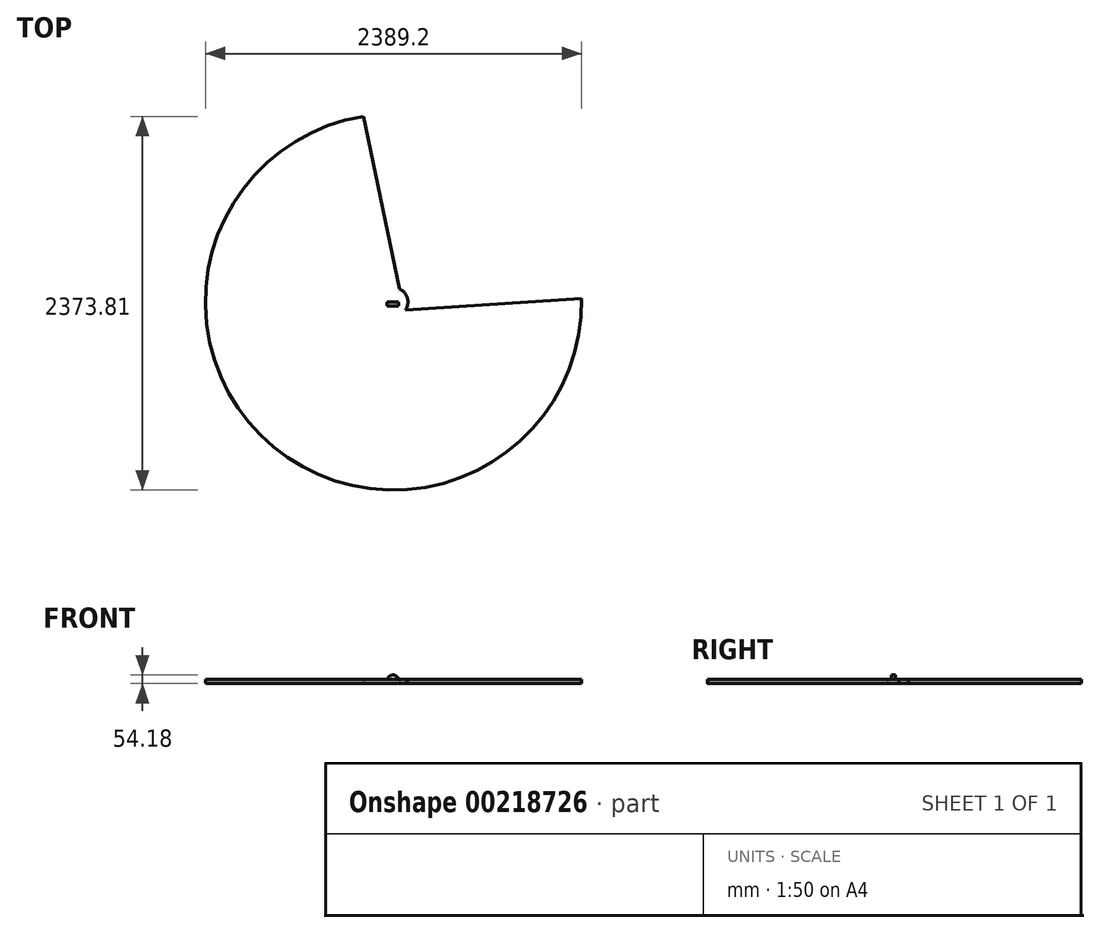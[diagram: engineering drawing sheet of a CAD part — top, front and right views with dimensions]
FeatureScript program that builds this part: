
annotation { "Feature Type Name" : "Feature", "Feature Type Description" : "" }
export const myFeature = defineFeature(function(context is Context, id is Id, definition is map)
    precondition{}
    {
        {
            var Q0;
            Q0=qCreatedBy(makeId("Front.planeOp"),FACE);
            var sketch = newSketch(context, id + "F0", { "sketchPlane" : qUnion([Q0])});
            skLineSegment(sketch, "E0", {"start": v(-39.47, 0) * mm, "end": v(-39.47, 19.73) * mm});
            skLineSegment(sketch, "E1", {"start": v(-39.47, 19.73) * mm, "end": v(-34.07, 19.73) * mm});
            skLineSegment(sketch, "E2", {"start": v(-34.07, 19.73) * mm, "end": v(-34.07, 0) * mm});
            skLineSegment(sketch, "E3", {"start": v(-39.47, 0) * mm, "end": v(-34.07, 0) * mm});
            skLineSegment(sketch, "E4", {"start": v(-34.07, 19.73) * mm, "end": v(26.7, 19.73) * mm});
            skLineSegment(sketch, "E5", {"start": v(26.7, 19.73) * mm, "end": v(26.7, 0) * mm});
            skLineSegment(sketch, "E6", {"start": v(26.7, 19.73) * mm, "end": v(32.94, 19.73) * mm});
            skLineSegment(sketch, "E7", {"start": v(32.94, 19.73) * mm, "end": v(32.94, 0) * mm});
            skLineSegment(sketch, "E8", {"start": v(26.7, 0) * mm, "end": v(32.94, 0) * mm});
            skLineSegment(sketch, "E9", {"start": v(-39.47, 19.73) * mm, "end": v(-39.47, 26.55) * mm});
            skLineSegment(sketch, "E10", {"start": v(-39.47, 26.55) * mm, "end": v(32.94, 26.55) * mm});
            skLineSegment(sketch, "E11", {"start": v(32.94, 26.55) * mm, "end": v(32.94, 17.46) * mm});
            skLineSegment(sketch, "E12", {"start": v(-7.67, 19.73) * mm, "end": v(-7.67, 0) * mm});
            skLineSegment(sketch, "E13", {"start": v(0, 19.73) * mm, "end": v(0, 0) * mm});
            skLineSegment(sketch, "E14", {"start": v(-7.67, 0) * mm, "end": v(1.99, 0) * mm});
            skArc(sketch, "E15", {"start": v(32.94, 26.55) * mm, "mid": v(-3.27, 54.18) * mm, "end": v(-39.47, 26.55) * mm});
            skSolve(sketch);
        }
        {
            var Q0;
            Q0 = qSketchRegion(id + "F0", true);
            extrude(context, id + "F1", {"entities" : qUnion([Q0]), "depth" : 25.4 * mm});
        }
        {
            var Q0;
            Q0=qCreatedBy(makeId("Top.planeOp"),FACE);
            var sketch = newSketch(context, id + "F2", { "sketchPlane" : qUnion([Q0])});
            skCircle(sketch, "E16", {"center": v(0, 0) * mm, "radius": 91.46 * mm});
            skLineSegment(sketch, "E17", {"start": v(-69.15, -59.86) * mm, "end": v(-55.1, -1159.97) * mm});
            skLineSegment(sketch, "E18", {"start": v(-54.33, -73.57) * mm, "end": v(-39.83, -1193.94) * mm});
            skLineSegment(sketch, "E19", {"start": v(-39.83, -1193.94) * mm, "end": v(-55.1, -1159.97) * mm});
            skLineSegment(sketch, "E20", {"start": v(50.64, -76.16) * mm, "end": v(69.07, -1159.97) * mm});
            skLineSegment(sketch, "E21", {"start": v(69.07, -59.95) * mm, "end": v(88.27, -1193.94) * mm});
            skLineSegment(sketch, "E22", {"start": v(69.07, -1159.97) * mm, "end": v(88.27, -1193.94) * mm});
            skSolve(sketch);
        }
        {
            var Q0;
            Q0 = qSketchRegion(id + "F2", true);
            extrude(context, id + "F3", {"entities" : qUnion([Q0]), "operationType" : NewBodyOperationType.ADD, "depth" : 25.4 * mm});
        }
        {
            var Q0;
            Q0=makeQuery(id+"F3.opExtrude","SWEPT_FACE",FACE,{"disambiguationData":[OSD([sQuery(id+"F2.wireOp",EDGE,"E18")])]});
            var Q1;
            {var subQ0=sQuery(id+"F2.wireOp",EDGE,"E16");Q1=makeQuery(id+"F3.opExtrude","CAP_EDGE",EDGE,{"disambiguationData":[OSD([subQ0]),TDD([makeQuery(id+"F2.imprint","IMPRINT",EDGE,{"disambiguationData":[TD([[makeQuery(id+"F2.imprint","INTERSECT",VERTEX,{"derivedFrom":[subQ0,sQuery(id+"F2.wireOp",EDGE,"E17")]}),1.0]])],"derivedFrom":subQ0})])],"isStart":true});}
            sweep(context, id + "F4", {"operationType" : NewBodyOperationType.ADD, "profiles" : qUnion([Q0]), "path" : qUnion([Q1])});
        }
        {
            var Q0;
            {var subQ0=sQuery(id+"F2.wireOp",EDGE,"E18");var subQ1=sQuery(id+"F2.wireOp",EDGE,"E17");var subQ2=sQuery(id+"F2.wireOp",EDGE,"E16");var subQ3=sQuery(id+"F2.wireOp",EDGE,"E21");Q0=makeQuery(id+"F4.boolean.opBoolean","MERGE",FACE,{"derivedFrom":[makeQuery(id+"F3.boolean.opBoolean","MERGE",FACE,{"derivedFrom":[makeQuery(id+"F1.opExtrude","SWEPT_FACE",FACE,{"disambiguationData":[OSD([sQuery(id+"F0.wireOp",EDGE,"E3")])]}),makeQuery(id+"F1.opExtrude","SWEPT_FACE",FACE,{"disambiguationData":[OSD([sQuery(id+"F0.wireOp",EDGE,"E8")])]}),makeQuery(id+"F1.opExtrude","SWEPT_FACE",FACE,{"disambiguationData":[OSD([sQuery(id+"F0.wireOp",EDGE,"E14")])]}),makeQuery(id+"F3.opExtrude","CAP_FACE",FACE,{"disambiguationData":[OSD([subQ2,subQ1,subQ0,sQuery(id+"F2.wireOp",EDGE,"E19"),sQuery(id+"F2.wireOp",EDGE,"E20"),subQ3,sQuery(id+"F2.wireOp",EDGE,"E22")])],"isStart":true})]}),makeQuery(id+"F4.opSweep","SWEPT_FACE",FACE,{"disambiguationData":[OSD([subQ2,subQ0]),TDD([makeQuery(id+"F3.opExtrude","CAP_EDGE",EDGE,{"disambiguationData":[OSD([subQ2]),TDD([makeQuery(id+"F2.imprint","IMPRINT",EDGE,{"disambiguationData":[TD([[makeQuery(id+"F2.imprint","INTERSECT",VERTEX,{"derivedFrom":[subQ2,subQ1]}),1.0]])],"derivedFrom":subQ2})])],"isStart":true}),makeQuery(id+"F3.opExtrude","CAP_EDGE",EDGE,{"disambiguationData":[OSD([subQ0])],"isStart":true})])]})]});}
            extrude(context, id + "F5", {"entities" : qUnion([Q0]), "operationType" : NewBodyOperationType.ADD, "oppositeDirection" : true, "depth" : 25.4 * mm});
        }
    });
